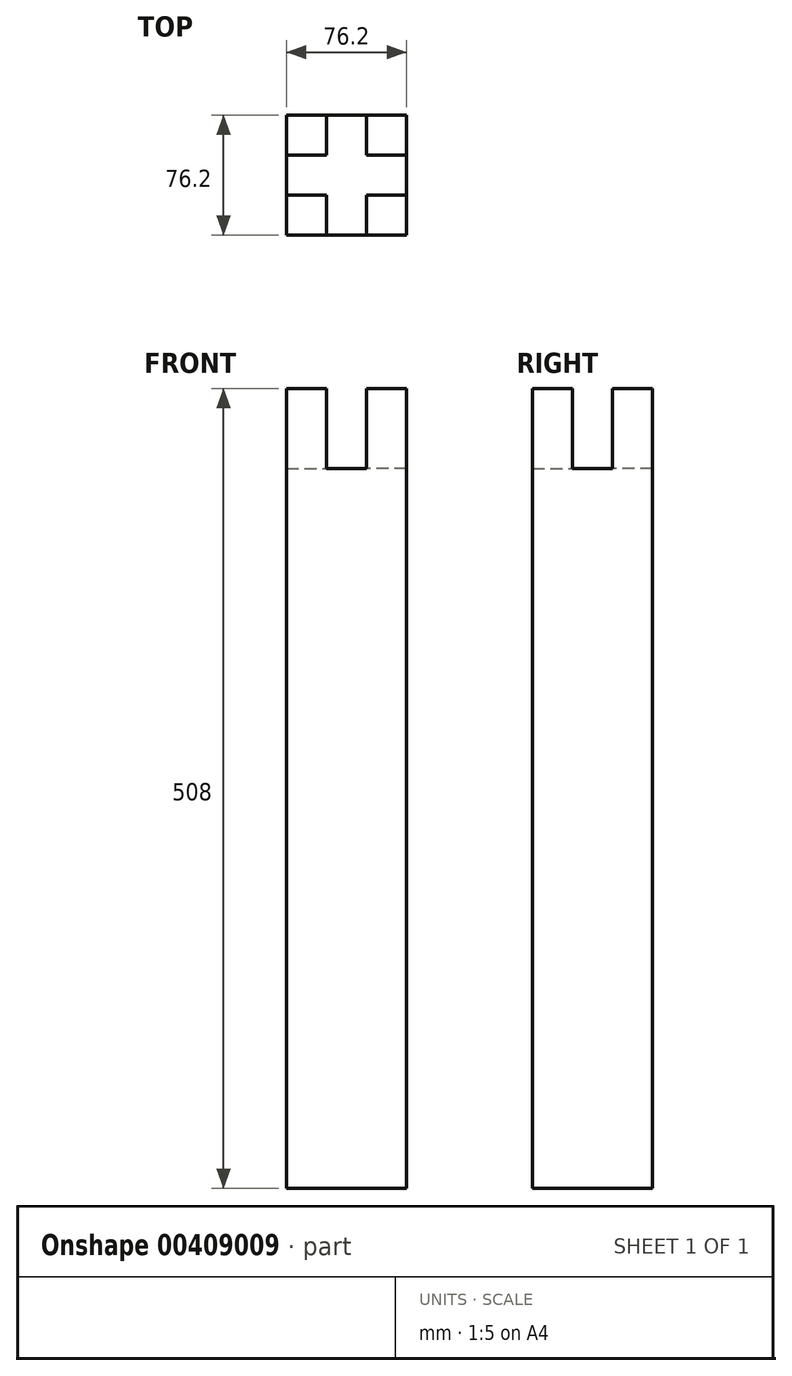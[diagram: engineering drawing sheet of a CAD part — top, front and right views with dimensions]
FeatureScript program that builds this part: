
annotation { "Feature Type Name" : "Feature", "Feature Type Description" : "" }
export const myFeature = defineFeature(function(context is Context, id is Id, definition is map)
    precondition{}
    {
        {
            var Q0;
            Q0=qCreatedBy(makeId("Front.planeOp"),FACE);
            var sketch = newSketch(context, id + "F0", { "sketchPlane" : qUnion([Q0])});
            skLineSegment(sketch, "E0.bottom", {"start": v(38.1, 254) * mm, "end": v(-38.1, 254) * mm});
            skLineSegment(sketch, "E0.top", {"start": v(38.1, -254) * mm, "end": v(-38.1, -254) * mm});
            skLineSegment(sketch, "E0.left", {"start": v(38.1, 254) * mm, "end": v(38.1, -254) * mm});
            skLineSegment(sketch, "E0.right", {"start": v(-38.1, 254) * mm, "end": v(-38.1, -254) * mm});
            skPoint(sketch, "E0.middle", {"position": v(0, 0) * mm});
            skSolve(sketch);
        }
        {
            var Q0;
            Q0=makeQuery(id+"F0.imprint","IMPRINT",FACE,{"disambiguationData":[TD([[makeQuery(id+"F0.imprint","IMPRINT",EDGE,{"derivedFrom":sQuery(id+"F0.wireOp",EDGE,"E0.bottom")}),1.0]])]});
            extrude(context, id + "F1", {"entities" : qUnion([Q0]), "depth" : 76.2 * mm});
        }
        {
            var Q0;
            Q0=makeQuery(id+"F1.opExtrude","SWEPT_FACE",FACE,{"disambiguationData":[OSD([sQuery(id+"F0.wireOp",EDGE,"E0.bottom")])]});
            var sketch = newSketch(context, id + "F2", { "sketchPlane" : qUnion([Q0])});
            skLineSegment(sketch, "E1.bottom", {"start": v(-38.1, 0) * mm, "end": v(-12.7, 0) * mm});
            skLineSegment(sketch, "E1.top", {"start": v(-38.1, -25.4) * mm, "end": v(-12.7, -25.4) * mm});
            skLineSegment(sketch, "E1.left", {"start": v(-38.1, 0) * mm, "end": v(-38.1, -25.4) * mm});
            skLineSegment(sketch, "E1.right", {"start": v(-12.7, 0) * mm, "end": v(-12.7, -25.4) * mm});
            skLineSegment(sketch, "E2.bottom", {"start": v(38.1, 0) * mm, "end": v(12.7, 0) * mm});
            skLineSegment(sketch, "E2.top", {"start": v(38.1, -25.4) * mm, "end": v(12.7, -25.4) * mm});
            skLineSegment(sketch, "E2.left", {"start": v(38.1, 0) * mm, "end": v(38.1, -25.4) * mm});
            skLineSegment(sketch, "E2.right", {"start": v(12.7, 0) * mm, "end": v(12.7, -25.4) * mm});
            skLineSegment(sketch, "E3.bottom", {"start": v(-38.1, -76.2) * mm, "end": v(-12.7, -76.2) * mm});
            skLineSegment(sketch, "E3.top", {"start": v(-38.1, -50.8) * mm, "end": v(-12.7, -50.8) * mm});
            skLineSegment(sketch, "E3.left", {"start": v(-38.1, -76.2) * mm, "end": v(-38.1, -50.8) * mm});
            skLineSegment(sketch, "E3.right", {"start": v(-12.7, -76.2) * mm, "end": v(-12.7, -50.8) * mm});
            skLineSegment(sketch, "E4.bottom", {"start": v(38.1, -76.2) * mm, "end": v(12.7, -76.2) * mm});
            skLineSegment(sketch, "E4.top", {"start": v(38.1, -50.8) * mm, "end": v(12.7, -50.8) * mm});
            skLineSegment(sketch, "E4.left", {"start": v(38.1, -76.2) * mm, "end": v(38.1, -50.8) * mm});
            skLineSegment(sketch, "E4.right", {"start": v(12.7, -76.2) * mm, "end": v(12.7, -50.8) * mm});
            skSolve(sketch);
        }
        {
            var Q0;
            {var subQ0=sQuery(id+"F2.wireOp",EDGE,"E1.top");Q0=makeQuery(id+"F2.imprint","IMPRINT",FACE,{"disambiguationData":[TD([[makeQuery(id+"F2.imprint","IMPRINT",EDGE,{"derivedFrom":subQ0}),-1.0]])]});}
            extrude(context, id + "F3", {"entities" : qUnion([Q0]), "operationType" : NewBodyOperationType.REMOVE, "oppositeDirection" : true, "depth" : 50.8 * mm});
        }
    });
